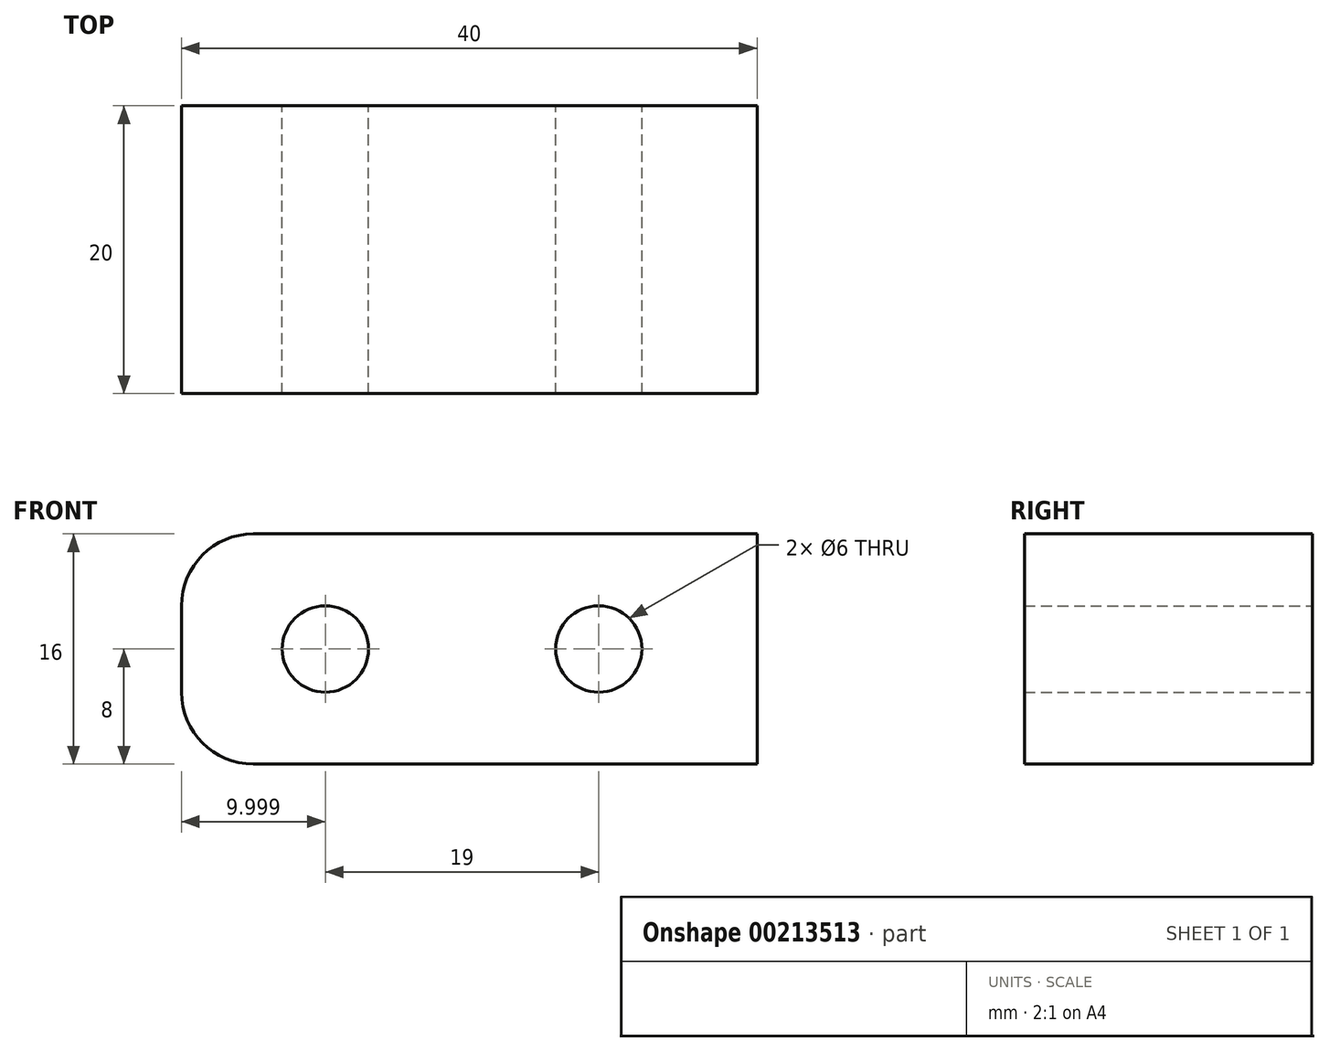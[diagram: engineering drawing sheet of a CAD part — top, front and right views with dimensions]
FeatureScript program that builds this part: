
annotation { "Feature Type Name" : "Feature", "Feature Type Description" : "" }
export const myFeature = defineFeature(function(context is Context, id is Id, definition is map)
    precondition{}
    {
        {
            var Q0;
            Q0=qCreatedBy(makeId("Front.planeOp"),FACE);
            var sketch = newSketch(context, id + "F0", { "sketchPlane" : qUnion([Q0])});
            skLineSegment(sketch, "E0.bottom", {"start": v(-18.02, 10.42) * mm, "end": v(21.98, 10.42) * mm});
            skLineSegment(sketch, "E0.top", {"start": v(-18.02, -5.58) * mm, "end": v(21.98, -5.58) * mm});
            skLineSegment(sketch, "E0.left", {"start": v(-18.02, 10.42) * mm, "end": v(-18.02, -5.58) * mm});
            skLineSegment(sketch, "E0.right", {"start": v(21.98, 10.42) * mm, "end": v(21.98, -5.58) * mm});
            skCircle(sketch, "E1", {"center": v(10.98, 2.42) * mm, "radius": 3 * mm});
            skPoint(sketch, "E1.centerSnap0", {"position": v(21.98, 2.42) * mm});
            skCircle(sketch, "E2", {"center": v(-8.02, 2.42) * mm, "radius": 3 * mm});
            skSolve(sketch);
        }
        {
            var Q0;
            Q0 = qSketchRegion(id + "F0", true);
            extrude(context, id + "F1", {"entities" : qUnion([Q0]), "depth" : 20 * mm});
        }
        {
            var Q0;
            Q0=makeQuery(id+"F1.opExtrude","SWEPT_EDGE",EDGE,{"disambiguationData":[OSD([sQuery(id+"F0.wireOp",EDGE,"E0.bottom"),sQuery(id+"F0.wireOp",EDGE,"E0.left")])]});
            var Q1;
            Q1=makeQuery(id+"F1.opExtrude","SWEPT_EDGE",EDGE,{"disambiguationData":[OSD([sQuery(id+"F0.wireOp",EDGE,"E0.top"),sQuery(id+"F0.wireOp",EDGE,"E0.left")])]});
            fillet(context, id + "F2", {"entities" : qUnion([Q0, Q1]), "radius" : 5 * mm, "tangentPropagation" : true, "allowEdgeOverflow" : false});
        }
    });
